# Revit family: Domotics-DomesticRanges-GEWISS-SYSTEM_COMMAND-PUSH-BUTTON
name_source: partatom
category: Apparecchi elettrici
revit_build: Autodesk Revit 2016 (Build: 20161004_0715(x64)
units: mm (PartAtom-declared; Revit-internal decimal feet)

## family parameters
Condiviso = Sì
Host = Superficie
Mantenere orientamento annotazione = Sì
Numero OmniClass = 23.80.50.11
Punto di calcolo locali = Sì
Quota connettore circolare = Usa diametro
Taglio con vuoti quando caricato = No
Tipo di parte = Normale
Titolo OmniClass = Switches and Receptacles

## types (30) — shared parameters
Bidimensionale = bidimensionale system pulsanti : 21531
Catalogue = DOMOTICS
Catalogue Range = SYSTEM - DOMESTIC RANGE
Electrocod = 0130
GW - N. moduli SYSTEM = 1
IDF = ccbc9b88-fa87-45ea-874a-d2a4544fd9ec
IDT = da59d091-0534-40ac-ae90-80184fb57ea1
Immagine tipo = GW21531.jpg
PULSANTE = GEWISS NERO
Produttore = GEWISS S.p.A.
Prospetto di default = 1219 mm
SEO = Push button
TIPO SIMBOLO = SIMBOLO PULSANTI : LUM
Technical sheet = https://www.gewiss.com
Tipo = SYSTEM PULSANTI_BASE : GW20531 Pulsante 1P NC 10A dischetto neutro Bianco
URL = https://www.gewiss.com
Version file RFA = 19.4
Voltage = 250 V ac
Voltage: = 250 V ac

## per-type parameters (varying)
| type | Button key | Description. | Description: | Descrizione | EAN code | GW - Caratteristiche | GW - Colore | GW - Simbolo | GW - Tipo | Modello |
| GW21513 - Push-button-1P NO 10A -light- black | With symbol | Push-button (NO) | 1P NO - 10A | PUSH-BUTTON-1P NA 10A -LIGHT- SY/BK | 8011564128071 | 1P NO - 10A | Black | Light | With symbol | GW21513 |
| GW20510 - Push-button-1P NO 10A white | Neutral | Push-button | 1P NO - 10A | PUSH-BUTTON-1P NO 10A SY/WT | 8011564077256 | 1P NO - 10A | White |  | General | GW20510 |
| GW21529 - Push-button-1P NO 10A -neutral- black | With replaceable neutral lens | Push-button | 1P NO - 10A illuminable | PUSH-BUTTON-1P NO 10A -NEUTRAL- SY/BK | 8011564128118 | 1P NO - 10A | Black |  | Illuminable | GW21529 |
| GW20517 - Push-button-2P NO 10A white | Neutral | Push-button (2P) | 2P NO - 10A | PUSH-BUTTON-2P NO 10A SY/WT | 8011564077355 | 2P NO - 10A | White | Double circle | General | GW20517 |
| GW21522 - Push-button-1P NO+aux NC -start- black | Start | Push-button (NO+NC) | 1P NO - 10A - Aux. NC | PUSH-BUTTON-1P NA+AUX NC -START- SY/BK | 8011564128156 | 1P NO - 10A - Aux. NC | Black | Green | Start | GW21522 |
| GW20519 - Push-button-1P NC 10A white | Neutral | Push-button (NC) | 1P NC - 10A | PUSH-BUTTON-1P NC 10A SY/WT | 8011564077317 | 1P NC - 10A | White | Circle | General | GW20519 |
| GW20521 - Push-button-1P NO+NO 10A v.arrow white | With interlock | Push-button | 1P NO+NO - 10A | PUSH-BUTTON-1P NO+NO 10A V.ARROW SY/WT | 8011564077324 | 1P NO+NO - 10A | White | UP - DOWN | With interlock | GW20521 |
| GW20516 - Push-button-1P NO 10A lum.12/24V white | With replaceable neutral lens | Push-button | 1P NO - 10 A backlit | PUSH-BUTTON-1P NO 10A LUM.12/24V SY/WT | 8011564081093 | 1P NO - 10A | White |  | Backlit 12/24V (0.8W) | GW20516 |
| GW21511 - Push-button-1P NO 10A -door- black | With symbol | Push-button (NO) | 1P NO - 10A | PUSH-BUTTON-1P NA 10A -DOOR- SY/BK | 8011564128057 | 1P NO - 10A | Black | Key | With symbol | GW21511 |
| GW21514 - Push-button-1P NO 10A -stair-black | With symbol | Push-button (NO) | 1P NO - 10A | PUSH-BUTTON-1P NA 10A -STAIR-SY/BK | 8011564128088 | 1P NO - 10A | Black | Stairs | With symbol | GW21514 |
| GW21512 - Push-button-1P NO 10A -ring- black | With symbol | Push-button (NO) | 1P NO - 10A | PUSH-BUTTON-1P NA 10A -RING- SY/BK | 8011564128064 | 1P NO - 10A | Black | Bell | With symbol | GW21512 |
| GW21521 - Push-button-1P NO+NO 10A v.arrow black | With interlock | Push-button | 1P NO+NO - 10A | PUSH-BUTTON-1P NA+NA 10A V.ARROW SY/BK | 8011564128149 | 1P NO+NO - 10A | Black | UP - DOWN | With interlock | GW21521 |
| GW21523 - Push-button-1P nC+aux NO -stop- black | Stop | Push-button (NC+NO) | 1P NC - 10A - Aux. NO | PUSH-BUTTON-1P NC+AUX NA -STOP- SY/BK | 8011564128163 | 1P NC - 10A - Aux. NO | Black | Red | Stop | GW21523 |
| GW21520 - Push-button-1P double NO 10A black | With interlock | Push-button (NO+NO) | 1P NO+NO - 10A | PUSH-BUTTON-1P DOUBLE NA 10A SY/BK | 8011564128132 | 1P NO+NO - 10A | Black | Double circles | With interlock | GW21520 |
| GW21519 - Push-button-1P NC 10A black | Neutral | Push-button (NC) | 1P NC - 10A | PUSH-BUTTON-1P NC 10A SY/BK | 8011564128125 | 1P NC - 10A | Black | Circle | General | GW21519 |
| GW20520 - Push-button-1P double NO 10A white | With interlock | Push-button (NO+NO) | 1P NO+NO - 10A | PUSH-BUTTON-1P DOUBLE NO 10A SY/WT | 8011564081109 | 1P NO+NO - 10A | White | Double circles | With interlock | GW20520 |
| GW21510 - Push-button-1P NO 10A black | Neutral | Push-button | 1P NO - 10A | PUSH-BUTTON-1P NA 10A SY/BK | 8011564128040 | 1P NO - 10A | Black |  | General | GW21510 |
| GW20514 - Push-button-1P NO 10A -stair-white | With symbol | Push-button (NO) | 1P NO - 10A | PUSH-BUTTON-1P NO 10A -STAIR-SY/WT | 8011564077294 | 1P NO - 10A | White | Stairs | With symbol | GW20514 |
| GW20512 - Push-button-1P NO 10A -ring- white | With symbol | Push-button (NO) | 1P NO - 10A | PUSH-BUTTON-1P NO 10A -RING- SY/WT | 8011564077270 | 1P NO - 10A | White | Bell | With symbol | GW20512 |
| GW20529 - Push-button-1P NO 10A -neutral- white | With replaceable neutral lens | Push-button | 1P NO - 10A illuminable | PUSH-BUTTON-1P NA 10A -NEUTRAL- SY/WT | 8011564077416 | 1P NO - 10A | White |  | Illuminable | GW20529 |
| GW21531 - Push-button-1P NC 10A -neutral- black | With replaceable neutral lens | Push-button | 1P NC - 10 A illuminable | PUSH-BUTTON-1P NC 10A -NEUTRAL- SY/BK | 8011564128286 | 1P NC - 10A | Black |  | Illuminable | GW21531 |
| GW20523 - Push-button-1P nC+aux NO -stop- white | Stop | Push-button (NC+NO) | 1P NC - 10A - Aux. NO | PUSH-BUTTON-1P NC+AUX NO -STOP- SY/WT | 8011564077348 | 1P NC - 10A - Aux. NO | White | Red | Stop | GW20523 |
| GW20522 - Push-button-1P NO+aux NC -start- white | Start | Push-button (NO+NC) | 1P NO - 10A - Aux. NC | PUSH-BUTTON-1P NO+AUX NC -START- SY/WT | 8011564077331 | 1P NO - 10A - Aux. NC | White | Green | Start | GW20522 |
| GW21516 - Push-button-1P NO 10A lum.12/24V black | With replaceable neutral lens | Push-button | 1P NO - 10 A backlit | PUSH-BUTTON-1P NA 10A LUM.12/24V SY/BK | 8011564128101 | 1P NO - 10A | Black |  | Backlit 12/24V (0.8W) | GW21516 |
| GW20511 - Push-button-1P NO 10A -door- white | With symbol | Push-button (NO) | 1P NO - 10A | PUSH-BUTTON-1P NO 10A -DOOR- SY/WT | 8011564077263 | 1P NO - 10A | White | Key | With symbol | GW20511 |
| GW20515 - Push-button-1P NO 10A lum.230V white | With replaceable neutral lens | Push-button | 1P NO - 10 A backlit | PUSH-BUTTON-1P NO 10A LUM.230V SY/WT | 8011564077300 | 1P NO - 10A | White |  | Backlit 230V ac (0.4W) | GW20515 |
| GW21517 - Push-button-2P NO 10A black | Neutral | Push-button (2P) | 2P NO - 10A | PUSH-BUTTON-2P NA 10A SY/BK | 8011564128170 | 2P NO - 10A | Black | Double circle | General | GW21517 |
| GW20513 - Push-button-1P NO 10A -light- white | With symbol | Push-button (NO) | 1P NO - 10A | PUSH-BUTTON-1P NO 10A -LIGHT- SY/WT | 8011564077287 | 1P NO - 10A | White | Light | With symbol | GW20513 |
| GW20531 - Push-button-1P NC 10A -neutral- white | With replaceable neutral lens | Push-button | 1P NC - 10 A illuminable | PUSH-BUTTON-1P NC 10A -NEUTRAL- SY/WT | 8011564077430 | 1P NC - 10A | White |  | Illuminable | GW20531 |
| GW21515 - Push-button-1P NO 10A lum.230V black | With replaceable neutral lens | Push-button | 1P NO - 10 A backlit | PUSH-BUTTON-1P NA 10A LUM.230V SY/BK | 8011564128095 | 1P NO - 10A | Black |  | Backlit 230V ac (0.4W) | GW21515 |

## geometry (parser evidence)
native form markers: Blend x4, Sweep x2
no freeform markers — native parametric forms only
